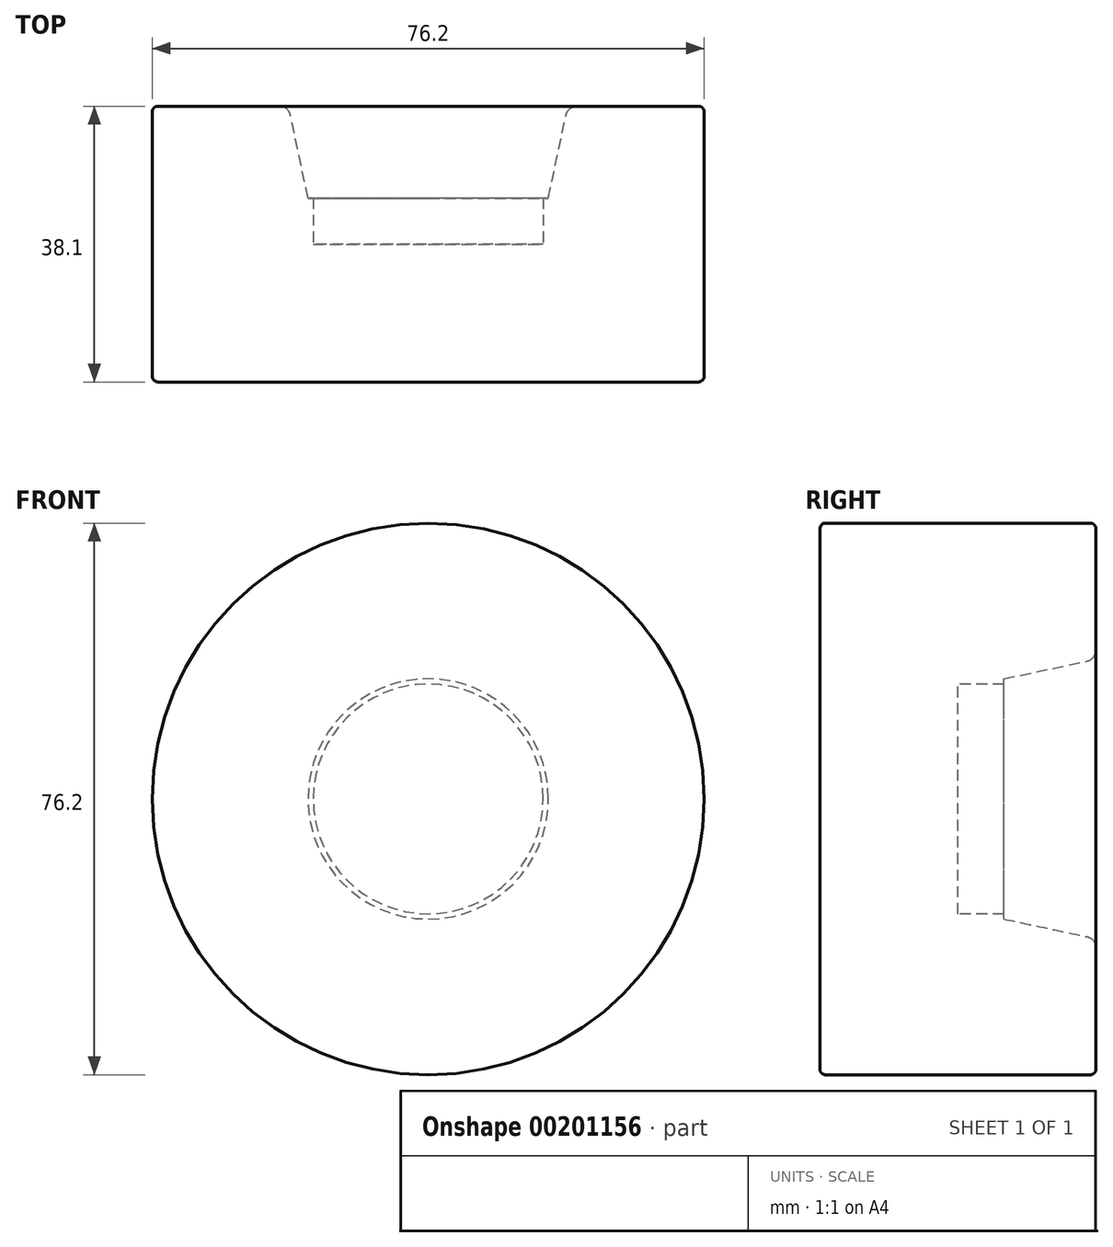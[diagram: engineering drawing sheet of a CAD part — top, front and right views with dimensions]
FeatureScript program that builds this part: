
annotation { "Feature Type Name" : "Feature", "Feature Type Description" : "" }
export const myFeature = defineFeature(function(context is Context, id is Id, definition is map)
    precondition{}
    {
        {
            var Q0;
            Q0=qCreatedBy(makeId("Right.planeOp"),FACE);
            var sketch = newSketch(context, id + "F0", { "sketchPlane" : qUnion([Q0])});
            skLineSegment(sketch, "E0", {"start": v(-12.7, 16.6) * mm, "end": v(-12.7, 15.87) * mm});
            skLineSegment(sketch, "E1", {"start": v(-12.7, 15.88) * mm, "end": v(-19.05, 15.88) * mm});
            skLineSegment(sketch, "E2", {"start": v(-19.05, 15.88) * mm, "end": v(-19.05, 0) * mm});
            skLineSegment(sketch, "E3", {"start": v(-0.76, 38.1) * mm, "end": v(-37.34, 38.1) * mm});
            skLineSegment(sketch, "E4", {"start": v(-38.1, 37.34) * mm, "end": v(-38.1, 0) * mm});
            skLineSegment(sketch, "E5", {"start": v(-38.1, 0) * mm, "end": v(-19.05, 0) * mm});
            skPoint(sketch, "E6.visualSharp", {"position": v(-38.1, 38.1) * mm});
            skArc(sketch, "E6.filletArc", {"start": v(-37.34, 38.1) * mm, "mid": v(-37.88, 37.88) * mm, "end": v(-38.1, 37.34) * mm});
            skPoint(sketch, "E7.visualSharp", {"position": v(0, 38.1) * mm});
            skArc(sketch, "E7.filletArc", {"start": v(0, 37.34) * mm, "mid": v(-0.22, 37.88) * mm, "end": v(-0.76, 38.1) * mm});
            skLineSegment(sketch, "E8", {"start": v(-12.7, 16.6) * mm, "end": v(-1.2, 19.04) * mm});
            skLineSegment(sketch, "E9", {"start": v(0, 37.34) * mm, "end": v(0, 20.53) * mm});
            skPoint(sketch, "E10.visualSharp", {"position": v(0, 19.3) * mm});
            skArc(sketch, "E10.filletArc", {"start": v(-1.2, 19.04) * mm, "mid": v(-0.34, 19.57) * mm, "end": v(0, 20.53) * mm});
            skSolve(sketch);
        }
        {
            var Q0;
            Q0 = qSketchRegion(id + "F0", true);
            var Q1;
            Q1=sQuery(id+"F0.wireOp",EDGE,"E5");
            revolve(context, id + "F1", {"entities" : qUnion([Q0]), "axis" : qUnion([Q1]), "revolveType" : RevolveType.FULL});
        }
    });
